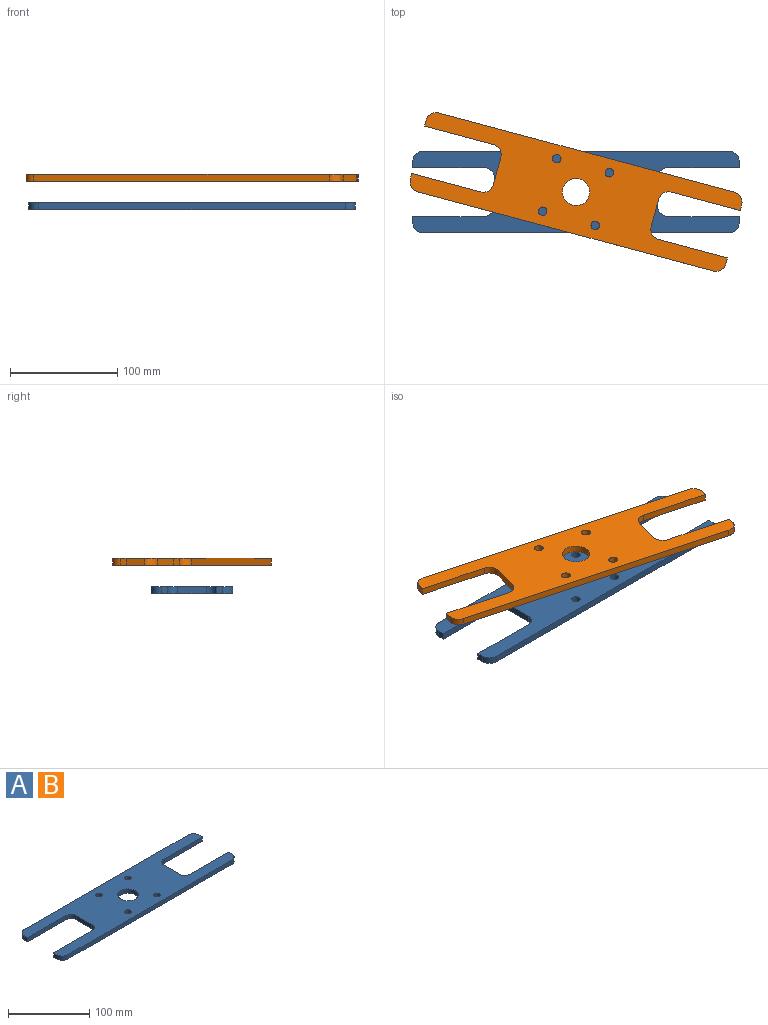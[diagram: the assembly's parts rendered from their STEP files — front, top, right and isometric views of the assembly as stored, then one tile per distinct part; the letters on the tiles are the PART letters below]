
ASSEMBLY  parts=2 mates=1
PART A: 27 faces, bbox 304.8x76.2x6.4 mm
  f0: plane 6.35x5.72mm, normal (1,0,0), area 36.3mm2, adj f2,f3,f7,f22
  f1: plane 6.35x5.72mm, normal (1,0,0), area 36.3mm2, adj f2,f3,f8,f23
  f2: plane 304.8x76.2mm, normal (0,0,1), area 15553.4mm2, adj f0,f1,f4,f5,f6,f7,f8,f9
  f3: plane 304.8x76.2mm, normal (0,0,-1), area 15553.4mm2, adj f0,f1,f4,f5,f6,f7,f8,f9
  f4: plane 6.35x5.72mm, normal (-1,0,0), area 36.3mm2, adj f2,f3,f10,f17
  f5: cylinder r=9.53mm len=9.53mm, axis (0,0,-1), area 95mm2, adj f2,f3,f6,f11
  f6: plane 285.75x6.35mm, normal (0,-1,0), area 1814.5mm2, adj f2,f3,f5,f7
  f7: cylinder r=9.53mm len=9.53mm, axis (0,0,-1), area 95mm2, adj f0,f2,f3,f6
  f8: cylinder r=9.53mm len=9.53mm, axis (0,0,-1), area 95mm2, adj f1,f2,f3,f9
  f9: plane 285.75x6.35mm, normal (0,1,0), area 1814.5mm2, adj f2,f3,f8,f10
  f10: cylinder r=9.53mm len=9.53mm, axis (0,0,-1), area 95mm2, adj f2,f3,f4,f9
  f11: plane 6.35x5.72mm, normal (-1,0,0), area 36.3mm2, adj f2,f3,f5,f18
  f12: cylinder r=12.7mm len=25.4mm, axis (0,0,1), area 506.7mm2, adj f2,f3
  f13: cylinder r=3.97mm len=7.94mm, axis (0,0,1), area 158.3mm2, adj f2,f3
  f14: cylinder r=3.97mm len=7.94mm, axis (0,0,1), area 158.3mm2, adj f2,f3
  f15: cylinder r=3.97mm len=7.94mm, axis (0,0,1), area 158.3mm2, adj f2,f3
  f16: cylinder r=3.97mm len=7.94mm, axis (0,0,1), area 158.3mm2, adj f2,f3
  f17: plane 66.68x6.35mm, normal (0,-1,0), area 423.4mm2, adj f2,f3,f4,f19
  f18: plane 66.68x6.35mm, normal (0,1,0), area 423.4mm2, adj f2,f3,f11,f21
  f19: cylinder r=9.53mm len=9.53mm, axis (0,0,1), area 95mm2, adj f2,f3,f17,f20
  f20: plane 26.67x6.35mm, normal (-1,0,0), area 169.4mm2, adj f2,f3,f19,f21
  f21: cylinder r=9.53mm len=9.53mm, axis (0,0,1), area 95mm2, adj f2,f3,f18,f20
  f22: plane 66.68x6.35mm, normal (0,1,0), area 423.4mm2, adj f0,f2,f3,f24
  f23: plane 66.68x6.35mm, normal (0,-1,0), area 423.4mm2, adj f1,f2,f3,f26
  f24: cylinder r=9.53mm len=9.53mm, axis (0,0,1), area 95mm2, adj f2,f3,f22,f25
  f25: plane 26.67x6.35mm, normal (1,0,0), area 169.4mm2, adj f2,f3,f24,f26
  f26: cylinder r=9.53mm len=9.53mm, axis (0,0,1), area 95mm2, adj f2,f3,f23,f25
PART B: same geometry as A
PLACE A at identity fixed
PLACE B rot(axis=(0,0,-1),15deg) t=(0,0,26.35)mm
MATE cylindrical A.f12 <-> B.f12  axis (0,0,1) through (0,0,6.35)mm
